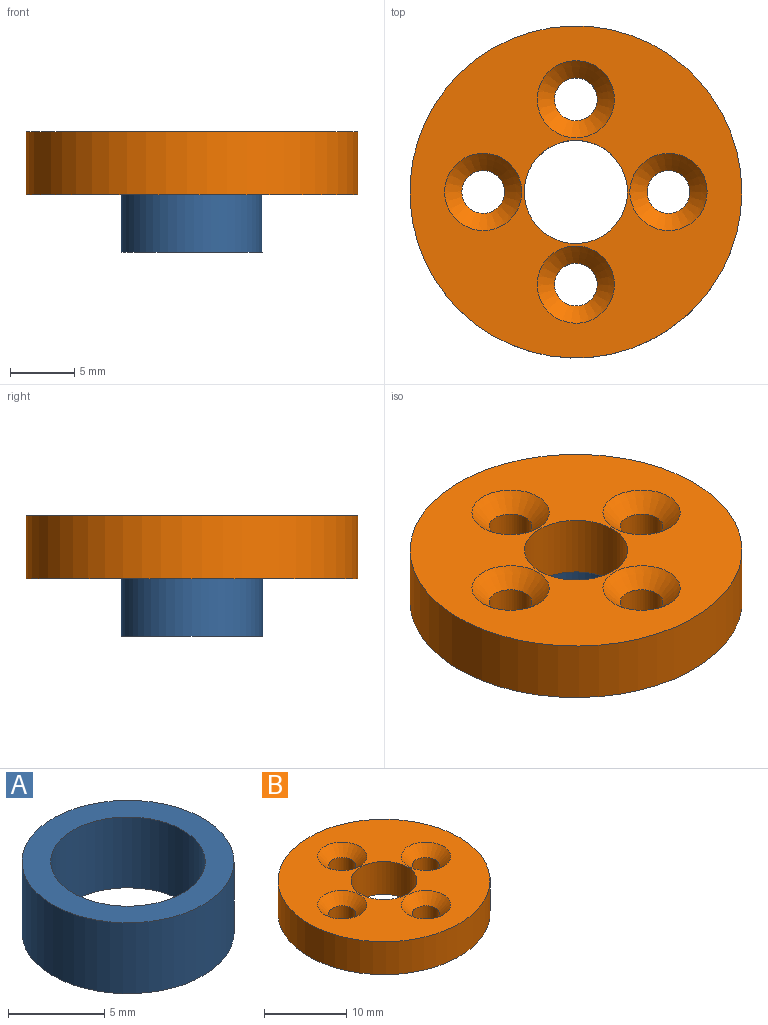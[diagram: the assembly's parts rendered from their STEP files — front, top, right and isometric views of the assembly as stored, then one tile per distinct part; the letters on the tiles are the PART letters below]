
ASSEMBLY  parts=2 mates=1
PART A: 4 faces, bbox 11x11x4.5 mm
  f0: cylinder r=4.01mm len=8.02mm, axis (0,0,1), area 113.3mm2, adj f2,f3
  f1: cylinder r=5.5mm len=11mm, axis (0,0,1), area 155.5mm2, adj f2,f3
  f2: plane 11x11mm, normal (0,0,-1), area 44.6mm2, adj f0,f1
  f3: plane 11x11mm, normal (0,0,1), area 44.6mm2, adj f0,f1
PART B: 12 faces, bbox 25.8x25.8x4.9 mm
  f0: cylinder r=1.66mm len=3.56mm, axis (0,0,1), area 37.1mm2, adj f6,f8
  f1: cylinder r=1.66mm len=3.56mm, axis (0,0,1), area 37.1mm2, adj f6,f10
  f2: cylinder r=1.66mm len=3.56mm, axis (0,0,1), area 37.1mm2, adj f6,f11
  f3: cylinder r=1.66mm len=3.56mm, axis (0,0,1), area 37.1mm2, adj f6,f9
  f4: cylinder r=12.9mm len=25.8mm, axis (0,0,1), area 397.2mm2, adj f6,f7
  f5: cylinder r=4.01mm len=8.02mm, axis (0,0,1), area 123.4mm2, adj f6,f7
  f6: plane 25.8x25.8mm, normal (0,0,-1), area 437.7mm2, adj f0,f1,f2,f3,f4,f5
  f7: plane 25.8x25.8mm, normal (0,0,1), area 359.2mm2, adj f4,f5,f8,f9,f10,f11
  f8: cone r=1mm half-angle=45deg, axis (0,0,1), area 27.7mm2, adj f0,f7
  f9: cone r=1mm half-angle=45deg, axis (0,0,1), area 27.7mm2, adj f3,f7
  f10: cone r=1mm half-angle=45deg, axis (0,0,1), area 27.7mm2, adj f1,f7
  f11: cone r=1mm half-angle=45deg, axis (0,0,1), area 27.7mm2, adj f2,f7
PLACE A t=(1.69,-0.72,-0.68)mm
PLACE B t=(1.69,-0.72,-0.68)mm
MATE fastened A.f0 <-> B.f5  axis (0,0,1) through (1.69,-0.72,-5.58)mm
